# Revit family: Serenity Series - Panel Wall - Recessed
name_source: partatom
category: Generic Models
units: mm (PartAtom-declared; Revit-internal decimal feet)

## family parameters
Always vertical = Yes
Can host rebar = No
Cut with Voids When Loaded = No
Part Type = Normal
Room Calculation Point = No
Round Connector Dimension = Use Diameter
Shared = No
Work Plane-Based = No

## types (12) — shared parameters
Base Offset = 0' - 8 7/8"
Ceiling Height = 8' - 0"
Center Panel & Frames = 3' - 11 3/8"
Front Frame Depth = 0' - 1 1/2"
Manufacturer = Amico Corporation
Model = Serenity Series Recessed PanelWall
Side Panel & Frames = 1' - 3 3/8"
Stud Height = 10' - 0"
Stud Size = 0' - 3 5/8"
URL = https://www.amico.com
Unit Height = 6' - 0 1/4"

## per-type parameters (varying)
| type | Inner Frame - no rail | Inner Frame - w/ Rail | Outer Frame - no rail | Outer Frame - w/ Rail | Panel - Full Frame | Panel - Inner Rails | Panel - Outer Rails | Panel - no frame | Stud Spacing |
| 14-48-14 - w/ rail | No | Yes | No | Yes | Yes | No | No | No | 1' - 2 3/8" |
| 19-48-19 - w/ rail | No | Yes | No | Yes | Yes | No | No | No | 1' - 7 3/8" |
| 24-48-24 - w/ rail | No | Yes | No | Yes | Yes | No | No | No | 1' - 10 7/8" |
| 14-48-14 - no rail | Yes | No | Yes | No | No | No | No | Yes | 1' - 2 3/8" |
| 19-48-19 - no rail | Yes | No | Yes | No | No | No | No | Yes | 1' - 7 3/8" |
| 24-48-24 - no rail | Yes | No | Yes | No | No | No | No | Yes | 1' - 10 7/8" |
| 14-48-14 - outer rail | Yes | No | No | Yes | No | No | Yes | No | 1' - 2 3/8" |
| 19-48-19- outer rail | Yes | No | No | Yes | No | No | Yes | No | 1' - 7 3/8" |
| 24-48-24 - Outer Rail | Yes | No | No | Yes | No | No | Yes | No | 1' - 10 7/8" |
| 14-48-14 - Inner Rail | No | Yes | Yes | No | No | Yes | No | No | 1' - 2 3/8" |
| 19-48-19- inner rail | No | Yes | Yes | No | No | Yes | No | No | 1' - 7 3/8" |
| 24-48-24 - inner rail | No | Yes | Yes | No | No | Yes | No | No | 1' - 10 7/8" |

## geometry (parser evidence)
native form markers: Blend x4, Sweep x42
no freeform markers — native parametric forms only
